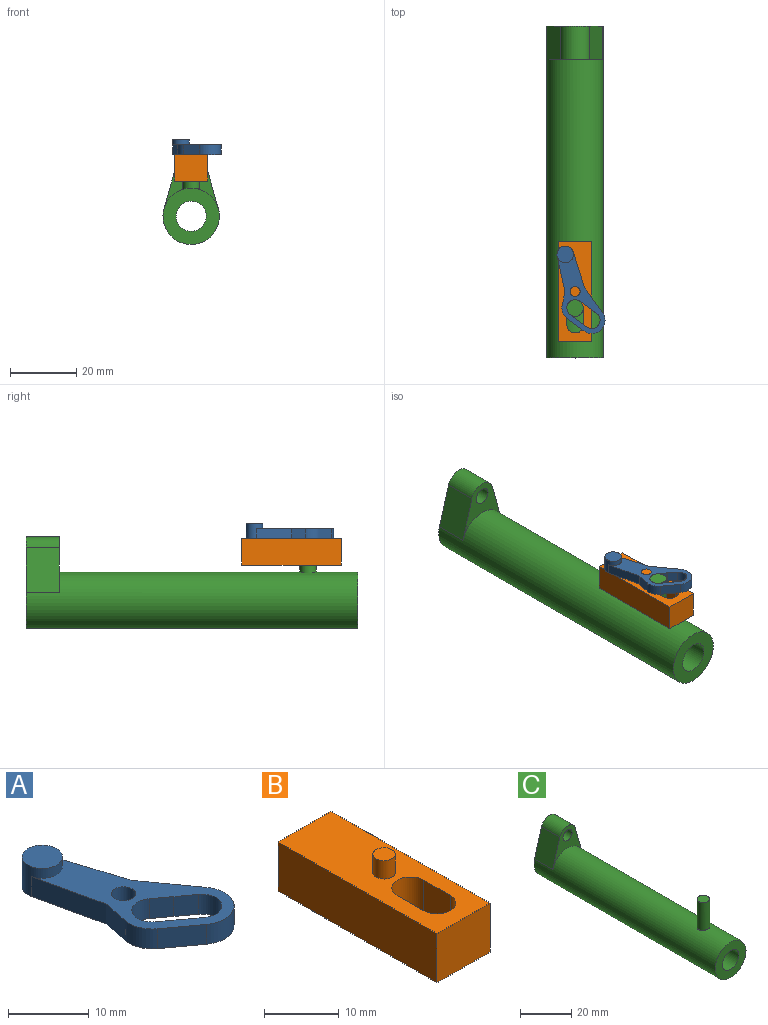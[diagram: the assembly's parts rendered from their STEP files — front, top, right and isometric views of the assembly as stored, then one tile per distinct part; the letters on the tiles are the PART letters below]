
ASSEMBLY  parts=3 mates=3
PART A: 22 faces, bbox 14.5x26.4x4.5 mm
  f0: cylinder r=4mm len=3mm, axis (0,0,-1), area 0.1mm2, adj f1,f18,f19,f20
  f1: cylinder r=4mm len=3mm, axis (0,0,-1), area 0.1mm2, adj f0,f2,f19,f20
  f2: plane 3x2.48mm, normal (-0.59,-0.81,0), area 9.2mm2, adj f1,f3,f19,f20
  f3: cylinder r=2.5mm len=4.52mm, axis (0,0,-1), area 23.6mm2, adj f2,f4,f19,f20
  f4: plane 3x2.48mm, normal (0.59,0.81,0), area 9.2mm2, adj f3,f5,f19,f20
  f5: cylinder r=4mm len=3mm, axis (0,0,-1), area 0.1mm2, adj f4,f6,f19,f20
  f6: cylinder r=4mm len=3mm, axis (0,0,-1), area 0.1mm2, adj f5,f7,f19,f20
  f7: plane 3x2.48mm, normal (0.59,0.81,0), area 9.2mm2, adj f6,f8,f19,f20
  f8: cylinder r=2.5mm len=4.52mm, axis (0,0,-1), area 23.6mm2, adj f7,f18,f19,f20
  f9: plane 10.68x3mm, normal (-0.98,-0.22,0), area 32.8mm2, adj f10,f17,f19,f20
  f10: plane 4.17x3mm, normal (-0.98,0.2,0), area 12.8mm2, adj f9,f11,f19,f20
  f11: cylinder r=4mm len=4.03mm, axis (0,0,-1), area 13.7mm2, adj f10,f12,f19,f20
  f12: plane 5x3.66mm, normal (-0.59,-0.81,0), area 18.6mm2, adj f11,f13,f19,f20
  f13: cylinder r=4mm len=6.36mm, axis (0,0,-1), area 33.9mm2, adj f12,f14,f19,f20
  f14: plane 7.68x5.53mm, normal (0.81,0.58,0), area 28.4mm2, adj f13,f15,f19,f20
  f15: plane 10.59x3.33mm, normal (0.95,0.3,0), area 33.3mm2, adj f14,f17,f19,f20
  f16: cylinder r=1.5mm len=3mm, axis (0,0,-1), area 28.3mm2, adj f19,f20
  f17: cylinder r=2.5mm len=5mm, axis (0,0,-1), area 46.5mm2, adj f9,f15,f19,f20,f21
  f18: plane 3x2.48mm, normal (-0.59,-0.81,0), area 9.2mm2, adj f0,f8,f19,f20
  f19: plane 24.61x14.44mm, normal (0,0,1), area 113.5mm2, adj f0,f1,f2,f3,f4,f5,f6,f7
  f20: plane 26.36x14.5mm, normal (0,0,-1), area 133.2mm2, adj f0,f1,f2,f3,f4,f5,f6,f7
  f21: plane 5x5mm, normal (0,0,1), area 19.6mm2, adj f17
PART B: 14 faces, bbox 10x30x11 mm
  f0: plane 10x8mm, normal (0,1,0), area 51.7mm2, adj f1,f7,f8,f9,f12
  f1: plane 30x8mm, normal (-1,0,0), area 240mm2, adj f0,f2,f8,f9
  f2: plane 10x8mm, normal (0,-1,0), area 80mm2, adj f1,f7,f8,f9
  f3: cylinder r=2.5mm len=8mm, axis (0,0,-1), area 62.8mm2, adj f4,f6,f8,f9
  f4: plane 8x5mm, normal (1,0,0), area 40mm2, adj f3,f5,f8,f9
  f5: cylinder r=2.5mm len=8mm, axis (0,0,-1), area 62.8mm2, adj f4,f6,f8,f9
  f6: plane 8x5mm, normal (-1,0,0), area 40mm2, adj f3,f5,f8,f9
  f7: plane 30x8mm, normal (1,0,0), area 240mm2, adj f0,f2,f8,f9
  f8: plane 30x10mm, normal (0,0,1), area 248.3mm2, adj f0,f1,f2,f3,f4,f5,f6,f7
  f9: plane 30x10mm, normal (0,0,-1), area 255.4mm2, adj f0,f1,f2,f3,f4,f5,f6,f7
  f10: cylinder r=1.5mm len=3mm, axis (0,0,-1), area 28.3mm2, adj f8,f11
  f11: plane 3x3mm, normal (0,0,1), area 7.1mm2, adj f10
  f12: cylinder r=3mm len=6mm, axis (0,1,0), area 94.2mm2, adj f0,f13
  f13: plane 6x6mm, normal (0,1,0), area 28.3mm2, adj f12
PART C: 12 faces, bbox 17x100x30.1 mm
  f0: cylinder r=8.5mm len=100mm, axis (0,1,0), area 5101mm2, adj f2,f3,f4,f6,f8,f10
  f1: cylinder r=4.55mm len=98.5mm, axis (0,1,0), area 2816mm2, adj f2,f9
  f2: plane 17x17mm, normal (0,-1,0), area 161.9mm2, adj f0,f1
  f3: plane 27.6x17mm, normal (0,1,0), area 207.6mm2, adj f0,f4,f5,f6,f7,f9
  f4: plane 13.5x10mm, normal (0.96,0,0.27), area 140.4mm2, adj f0,f3,f5,f8
  f5: cylinder r=4.5mm len=10mm, axis (0,1,0), area 116.4mm2, adj f3,f4,f6,f8
  f6: plane 13.5x10mm, normal (-0.96,0,0.27), area 140.4mm2, adj f0,f3,f5,f8
  f7: cylinder r=2.5mm len=10mm, axis (0,1,0), area 157.1mm2, adj f3,f8
  f8: plane 16.77x16.35mm, normal (0,-1,0), area 95.7mm2, adj f0,f4,f5,f6,f7
  f9: cone r=6.05mm half-angle=45deg, axis (0,1,0), area 70.6mm2, adj f1,f3
  f10: cylinder r=2.5mm len=13.48mm, axis (0,0,-1), area 208.7mm2, adj f0,f11
  f11: plane 5x5mm, normal (0,0,1), area 19.6mm2, adj f10
PLACE A t=(2.62,-78.51,18.28)mm
PLACE B t=(2.62,-78.51,10.28)mm
PLACE C t=(2.62,1.49,-0.32)mm
MATE pin_slot C.f10 <-> A.f8  axis (0,0,1) through (2.62,-83.51,21.28)mm
MATE pin_slot C.f10 <-> B.f3  axis (0,0,1) through (2.62,-83.51,21.28)mm
MATE revolute A.f16 <-> B.f10  axis (0,0,1) through (2.62,-78.51,21.28)mm
